AUTODESK INVENTOR PART (.ipt)
format: ipt  version: 2023.1 (Build 271208000, 208)  size: 81,920 bytes
history: native  units: in
note: dims shown in document units (in); Inventor stores cm internally (conversion verified against a paired STEP export)
features: sketch x2
ambient origin geometry x8: Origin, YZ Plane, XZ Plane, XY Plane, X Axis, Y Axis, Z Axis, Center Point
feature tree (2):
  sketch  "Sketch1"  dims[d0=0.375in]
  sketch  "Sketch2"  dims[d1=3.1496in d2=0.75in d3=2.75in d5=1.6in d6=3.2in d7=45.0deg d8=0.1875in d9=0.1in d10=1.5748in d12=360.0deg]
